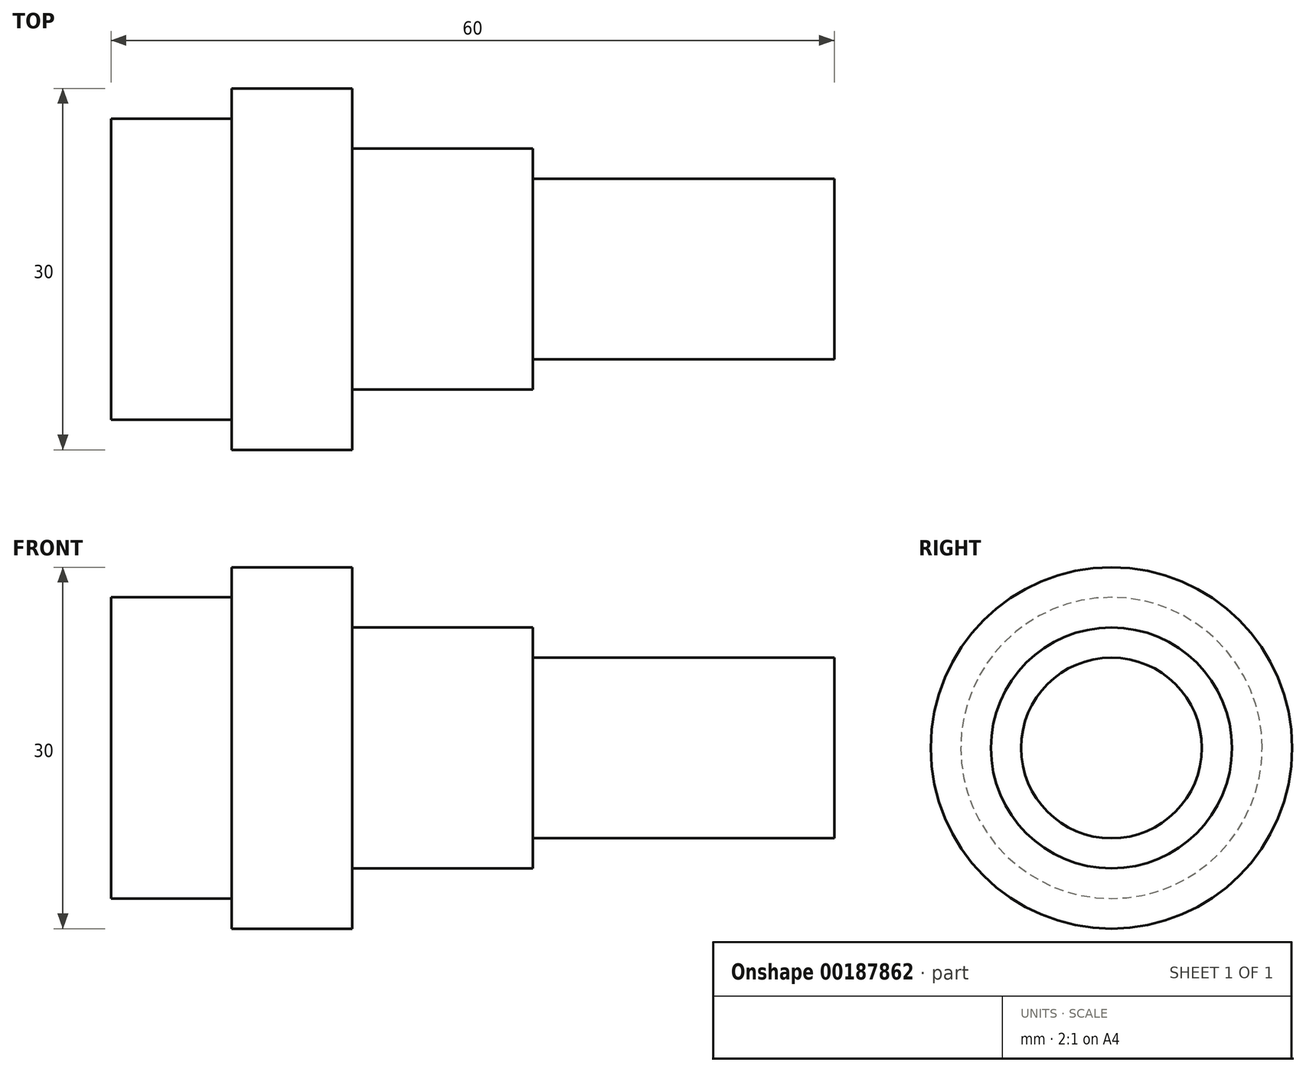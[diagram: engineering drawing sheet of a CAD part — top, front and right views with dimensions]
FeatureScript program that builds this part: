
annotation { "Feature Type Name" : "Feature", "Feature Type Description" : "" }
export const myFeature = defineFeature(function(context is Context, id is Id, definition is map)
    precondition{}
    {
        {
            var Q0;
            Q0=qCreatedBy(makeId("Front.planeOp"),FACE);
            var sketch = newSketch(context, id + "F0", { "sketchPlane" : qUnion([Q0])});
            skLineSegment(sketch, "E0", {"start": v(0, 0) * mm, "end": v(60, 0) * mm});
            skLineSegment(sketch, "E1", {"start": v(60, 0) * mm, "end": v(60, 7.5) * mm});
            skLineSegment(sketch, "E2", {"start": v(60, 7.5) * mm, "end": v(35, 7.5) * mm});
            skLineSegment(sketch, "E3", {"start": v(35, 7.5) * mm, "end": v(35, 10) * mm});
            skLineSegment(sketch, "E4", {"start": v(35, 10) * mm, "end": v(20, 10) * mm});
            skLineSegment(sketch, "E5", {"start": v(20, 10) * mm, "end": v(20, 15) * mm});
            skLineSegment(sketch, "E6", {"start": v(20, 15) * mm, "end": v(10, 15) * mm});
            skLineSegment(sketch, "E7", {"start": v(10, 15) * mm, "end": v(10, 12.5) * mm});
            skLineSegment(sketch, "E8", {"start": v(10, 12.5) * mm, "end": v(0, 12.5) * mm});
            skLineSegment(sketch, "E9", {"start": v(0, 12.5) * mm, "end": v(0, 0) * mm});
            skSolve(sketch);
        }
        {
            var Q0;
            Q0=makeQuery(id+"F0.imprint","IMPRINT",FACE,{"disambiguationData":[TD([[makeQuery(id+"F0.imprint","IMPRINT",EDGE,{"derivedFrom":sQuery(id+"F0.wireOp",EDGE,"E0")}),1.0]])]});
            var Q1;
            Q1=sQuery(id+"F0.wireOp",EDGE,"E0");
            revolve(context, id + "F1", {"entities" : qUnion([Q0]), "axis" : qUnion([Q1]), "revolveType" : RevolveType.FULL});
        }
    });
